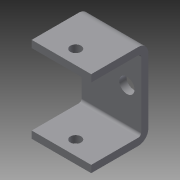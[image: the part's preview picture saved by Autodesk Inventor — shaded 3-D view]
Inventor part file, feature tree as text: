
AUTODESK INVENTOR PART (.ipt)
format: ipt  version: 2013 (Build 170138000, 138)  size: 128,512 bytes
history: native  units: in
note: dims shown in document units (in); Inventor stores cm internally (conversion verified against a paired STEP export)
features: sheet_metal_op x4, sketch x4, other x3, reference x2, extrude x1
ambient origin geometry x8: Origin, YZ Plane, XZ Plane, XY Plane, X Axis, Y Axis, Z Axis, Center Point
bodies: Solid1 (feature_tree)
feature tree (14):
  sheet_metal_op  "Face1"
  sheet_metal_op  "Flange1"
  extrude  "Extrusion1"  Depth=1.15in
  sketch  "Sketch1"  dims[d4=0.5788in d5=1.15in]
  other  "Plate1"
  sketch  "Sketch2"  dims[d6=0.125in]
  other  "Plate2"
  sheet_metal_op  "Bend1"
  sheet_metal_op  "Corner1"
  sketch  "Sketch3"  dims[d7=0.125in]
  sketch  "Sketch5"  dims[d8=0.0625in d9=0.25in d10=0.125in d11=1.0in d12=90.0deg d13=0.05in d14=0.5in d15=0.125in d16=0.125in d17=0.25in d18=0.1875in d19=2999.0in d20=0.0in d21=0.575in d22=0.125in d23=0.0in]
  reference  "Reference1"
  reference  "Reference2"
  other  "Cut1"
